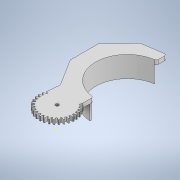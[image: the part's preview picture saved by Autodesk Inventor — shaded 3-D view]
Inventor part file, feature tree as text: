
AUTODESK INVENTOR PART (.ipt)
format: ipt  version: 2021 (Build 250183000, 183)  size: 544,256 bytes
history: native  units: mm
features: sketch x14, extrude x12, fillet x10
ambient origin geometry x8: Origin, YZ Plane, XZ Plane, XY Plane, X Axis, Y Axis, Z Axis, Center Point
bodies: Solid1 (feature_tree)
feature tree (36):
  extrude  "Extrusion1"  Depth=35.0mm
  extrude  "Extrusion4"  Depth=0.5mm
  extrude  "Extrusion6"  Depth=0.1mm TaperAngle=360.0deg
  extrude  "Extrusion9"  Depth=0.1mm
  fillet  "Fillet11"  Radius=10.0mm
  fillet  "Fillet12"  Radius=4.0mm
  fillet  "Fillet13"  Radius=10.0mm
  fillet  "Fillet14"  Radius=0.1mm
  sketch  "Sketch18"  dims[d65=2.0mm d66=2.0mm d67=2.0mm d68=2.0mm d11=0.5mm d12=0.872665mm d64=0.5mm]
  extrude  "Extrusion10"  Depth=2.0mm TaperAngle=0.0deg
  extrude  "Extrusion11"  Depth=10.0mm
  fillet  "Fillet4"  Radius=10.0mm
  sketch  "Sketch14"  dims[d55=1614.0mm d56=30.0mm]
  extrude  "Extrusion12"  Depth=10.0mm TaperAngle=0.0deg
  fillet  "Fillet5"  Radius=20.0mm
  fillet  "Fillet6"  Radius=22.0mm
  fillet  "Fillet7"  Radius=5.0mm
  fillet  "Fillet8"  Radius=40.0mm
  extrude  "Extrusion13"  Depth=20.0mm
  fillet  "Fillet9"  Radius=20.0mm
  extrude  "Extrusion14"  Depth=4.0mm TaperAngle=0.0deg
  extrude  "Extrusion5"  Depth=30.0mm
  extrude  "Extrusion2"  Depth=2.0mm
  extrude  "Extrusion3"  Depth=4.0mm
  sketch  "Sketch1"  dims[d0=30.0mm d1=35.0mm]
  sketch  "Sketch2"  dims[d2=0.5mm d4=0.5mm]
  sketch  "Sketch3"  dims[d6=0.1mm d7=310.0mm d9=360.0deg]
  sketch  "Sketch4"  dims[d13=60.0mm d14=30.0mm d15=10.0mm d19=4.0mm d20=0.0mm d22=10.0mm d23=0.1mm]
  sketch  "Sketch5"  dims[d24=2.0mm d25=3.0mm d26=0.0mm]
  sketch  "Sketch6"  dims[d27=3.0mm d28=0.0mm d29=3.0mm d30=10.0mm d31=0.0mm]
  sketch  "Sketch10"  dims[d32=40.0mm d33=10.0mm d34=0.0mm d35=20.0mm d36=0.0mm d43=22.0mm d44=5.0mm d45=0.0mm d46=40.0mm]
  sketch  "Sketch12"  dims[d47=4.0mm d48=0.0mm d49=40.0mm d50=20.0mm d51=0.0mm]
  sketch  "Sketch13"  dims[d52=21.0mm d53=4.0mm d54=0.0mm]
  sketch  "Sketch15"  dims[d57=2.0mm d58=2.0mm]
  sketch  "Sketch16"  dims[d59=4.0mm d60=0.0mm d61=2.25mm]
  sketch  "Sketch17"  dims[d62=20.0mm d63=0.0mm]
